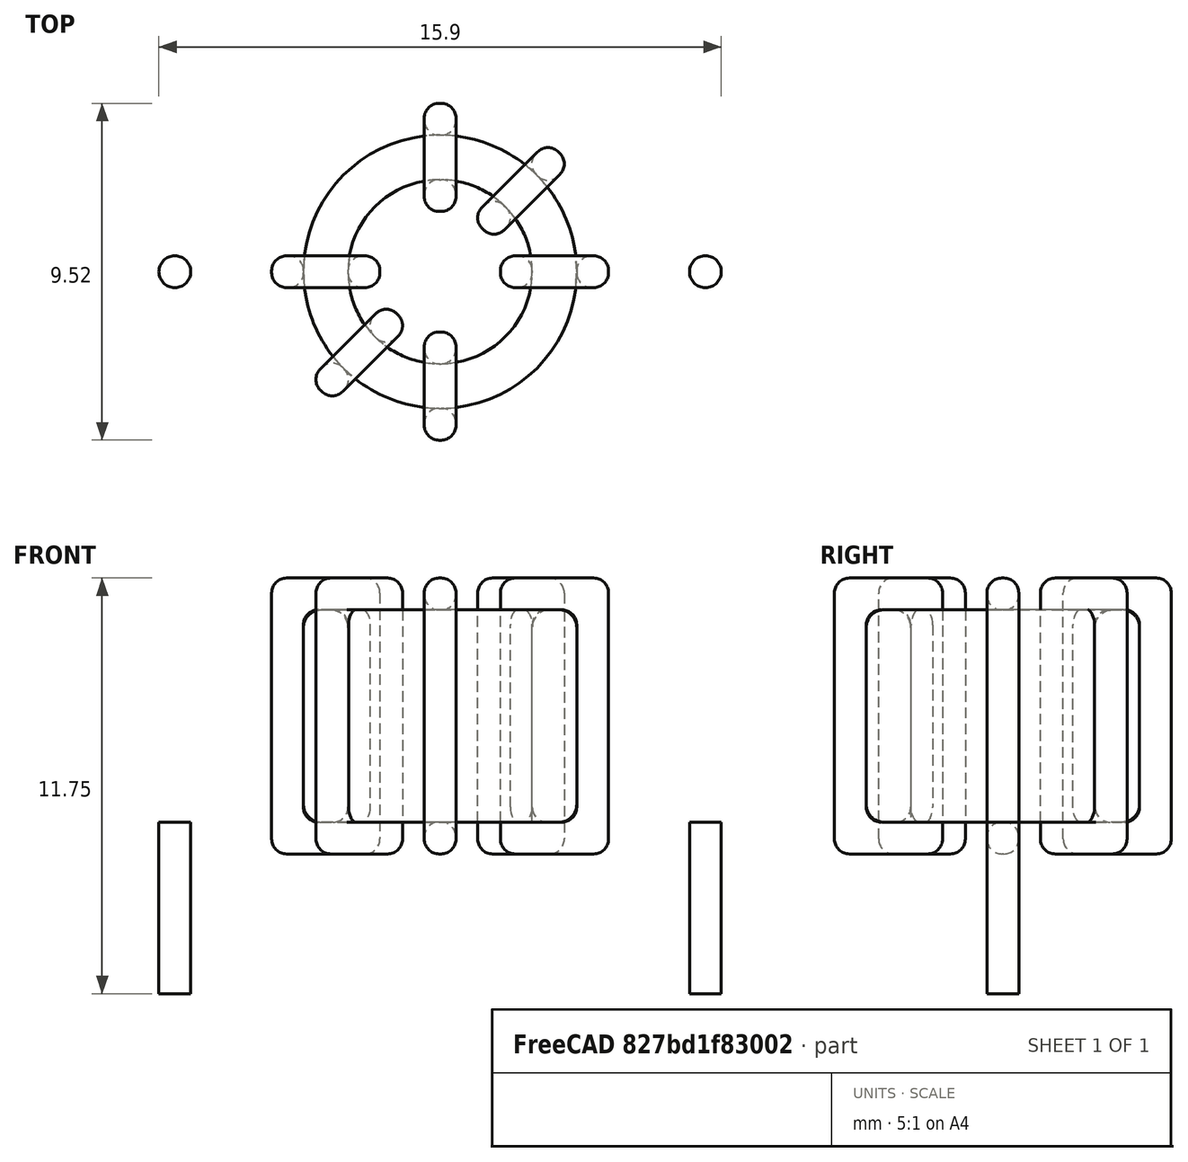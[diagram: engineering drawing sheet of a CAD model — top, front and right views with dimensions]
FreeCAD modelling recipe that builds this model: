
FCSTD DOCUMENT  (FreeCAD 0.16R6703 (Git))
Label: L_Toroid_Horizontal_D9.5mm_P15.00mm_Diameter10-5mm_Amidon-T37
License: All rights reserved
LicenseURL: http://en.wikipedia.org/wiki/All_rights_reserved
objects: Sketcher::SketchObject×6, PartDesign::Pad×6, PartDesign::Fillet×5, Spreadsheet::Sheet×1
note: 23 computed .brp shape members not serialized (recipe doc carries the construction recipe); baked Part::Feature solids carry a one-line shape summary decoded from their .brp

FEATURE [Spreadsheet::Sheet] Spreadsheet  label="dimensions"
  cells = A1=Wx; B1(Wx)=9.524999999999999; C1(WW)=5.206999999999999; D1=9.524999999999999; A2=Wy; B2(Wy)=9.524999999999999; D2=9.524999999999999; A3=RM; B3(RMx)=15; C3(RMy)=0; A4=d_wire; B4(d_wire)=0.8999999999999999; A5=H; B5(H)=6; A6=offsetx; B6(offsetx)=-2.737500000000001
FEATURE [Sketcher::SketchObject] Sketch
  Placement = pos=(0,0,1.4) rot=(0,0,1;0rad)
  expr: Placement.Base.z = 0.5 + Spreadsheet.d_wire
  expr: Constraints[0] = Spreadsheet.Wx / 2 - Spreadsheet.d_wire
  expr: Constraints[4] = Spreadsheet.WW / 2
  expr: Constraints[2] = Spreadsheet.RMy / 2
  expr: Constraints[1] = Spreadsheet.RMx / 2
  sketch-geometry (2):
    g0: Circle CenterX=7.5 CenterY=0 CenterZ=0 NormalX=0 NormalY=0 NormalZ=1 Radius=3.8625
    g1: Circle CenterX=7.5 CenterY=0 CenterZ=0 NormalX=0 NormalY=0 NormalZ=1 Radius=2.6035
  constraints (5):
    c: Radius(g0) = 3.8625
    c: DistanceX(g-1,g0) = 7.5
    c: DistanceY(g-1,g0) = 0
    c: Coincident(g1,g0)
    c: Radius(g1) = 2.6035
FEATURE [PartDesign::Pad] Pad
  Length = 6
  Length2 = 100
  Placement = pos=(0,0,1.4) rot=(0,0,1;0rad)
  Sketch = -> Sketch
  Type = 0
  expr: Length = Spreadsheet.H
FEATURE [Sketcher::SketchObject] Sketch001
  Placement = pos=(0,0,0.95) rot=(0,0,1;0rad)
  expr: Placement.Base.z = 0.5 + Spreadsheet.d_wire * 0.5
  expr: Constraints[4] = Spreadsheet.RMx
  expr: Constraints[2] = Spreadsheet.RMy
  expr: Constraints[1] = Spreadsheet.d_wire / 2
  sketch-geometry (2):
    g0: Circle CenterX=0 CenterY=0 CenterZ=0 NormalX=0 NormalY=0 NormalZ=1 Radius=0.45
    g1: Circle CenterX=15 CenterY=0 CenterZ=0 NormalX=0 NormalY=0 NormalZ=1 Radius=0.45
  constraints (5):
    c: Equal(g0,g1)
    c: Radius(g0) = 0.45
    c: DistanceY(g-1,g1) = 0
    c: Coincident(g0,g-1)
    c: DistanceX(g-1,g1) = 15
FEATURE [PartDesign::Pad] Pad001
  Length = 0.45
  Length2 = 4.4
  Placement = pos=(0,0,0.95) rot=(0,0,1;0rad)
  Reversed = true
  Sketch = -> Sketch001
  Type = 4
  expr: Length2 = 3.5 + Spreadsheet.d_wire
  expr: Length = Spreadsheet.d_wire / 2
FEATURE [PartDesign::Fillet] Fillet
  Base = -> Pad [Edge6,Edge3,Edge2]
  Placement = pos=(0,0,1.4) rot=(0,0,1;0rad)
  Radius = 0.5
FEATURE [Sketcher::SketchObject] Sketch003
  Placement = pos=(7.5,0,0) rot=(1,0,0;1.5708rad)
  expr: Placement.Base.x = Spreadsheet.RMx / 2
  expr: Constraints[49] = Spreadsheet.Wx - Spreadsheet.d_wire * 2
  expr: Constraints[44] = Spreadsheet.d_wire
  expr: Constraints[23] = Spreadsheet.H
  expr: Constraints[22] = Spreadsheet.Wx / 2 - Spreadsheet.d_wire
  expr: Placement.Base.y = Spreadsheet.RMy / 2
  expr: Constraints[21] = (Spreadsheet.Wx - Spreadsheet.WW) / 2 - Spreadsheet.d_wire
  expr: Constraints[19] = Spreadsheet.d_wire
  expr: Constraints[17] = Spreadsheet.d_wire
  expr: Constraints[18] = Spreadsheet.d_wire
  expr: Constraints[16] = Spreadsheet.d_wire
  sketch-geometry (16):
    g0: LineSegment StartX=-1.7035 StartY=0.5 StartZ=0 EndX=-4.7625 EndY=0.5 EndZ=0
    g1: LineSegment StartX=-4.7625 StartY=0.5 StartZ=0 EndX=-4.7625 EndY=8.3 EndZ=0
    g2: LineSegment StartX=-4.7625 StartY=8.3 StartZ=0 EndX=-1.7035 EndY=8.3 EndZ=0
    g3: LineSegment StartX=-1.7035 StartY=8.3 StartZ=0 EndX=-1.7035 EndY=0.5 EndZ=0
    g4: LineSegment StartX=-3.8625 StartY=7.4 StartZ=0 EndX=-2.6035 EndY=7.4 EndZ=0
    g5: LineSegment StartX=-2.6035 StartY=7.4 StartZ=0 EndX=-2.6035 EndY=1.4 EndZ=0
    g6: LineSegment StartX=-2.6035 StartY=1.4 StartZ=0 EndX=-3.8625 EndY=1.4 EndZ=0
    g7: LineSegment StartX=-3.8625 StartY=1.4 StartZ=0 EndX=-3.8625 EndY=7.4 EndZ=0
    g8: LineSegment StartX=1.7035 StartY=8.3 StartZ=0 EndX=4.7625 EndY=8.3 EndZ=0
    g9: LineSegment StartX=4.7625 StartY=8.3 StartZ=0 EndX=4.7625 EndY=0.5 EndZ=0
    g10: LineSegment StartX=4.7625 StartY=0.5 StartZ=0 EndX=1.7035 EndY=0.5 EndZ=0
    g11: LineSegment StartX=1.7035 StartY=0.5 StartZ=0 EndX=1.7035 EndY=8.3 EndZ=0
    g12: LineSegment StartX=2.6035 StartY=7.4 StartZ=0 EndX=3.8625 EndY=7.4 EndZ=0
    g13: LineSegment StartX=3.8625 StartY=7.4 StartZ=0 EndX=3.8625 EndY=1.4 EndZ=0
    g14: LineSegment StartX=3.8625 StartY=1.4 StartZ=0 EndX=2.6035 EndY=1.4 EndZ=0
    g15: LineSegment StartX=2.6035 StartY=1.4 StartZ=0 EndX=2.6035 EndY=7.4 EndZ=0
  constraints (50):
    c: Horizontal(g0)
    c: Coincident(g1,g0)
    c: Vertical(g1)
    c: Coincident(g2,g1)
    c: Horizontal(g2)
    c: Coincident(g3,g2)
    c: Coincident(g3,g0)
    c: Vertical(g3)
    c: Coincident(g4,g5)
    c: Coincident(g5,g6)
    c: Coincident(g6,g7)
    c: Coincident(g7,g4)
    c: Horizontal(g4)
    c: Horizontal(g6)
    c: Vertical(g5)
    c: Vertical(g7)
    c: DistanceX(g1,g4) = 0.9
    c: DistanceY(g4,g1) = 0.9
    c: DistanceX(g5,g0) = 0.9
    c: DistanceY(g0,g5) = 0.9
    c: DistanceY(g-1,g0) = 0.5
    c: DistanceX(g6,g6) = 1.259
    c: DistanceX(g6,g-1) = 3.8625
    c: DistanceY(g7,g7) = 6
    c: Coincident(g8,g9)
    c: Coincident(g9,g10)
    c: Coincident(g10,g11)
    c: Coincident(g11,g8)
    c: Horizontal(g8)
    c: Horizontal(g10)
    c: Vertical(g9)
    c: Vertical(g11)
    c: Coincident(g12,g13)
    c: Coincident(g13,g14)
    c: Coincident(g14,g15)
    c: Coincident(g15,g12)
    c: Horizontal(g12)
    c: Horizontal(g14)
    c: Vertical(g13)
    c: Vertical(g15)
    c: DistanceY(g8,g2) = 0
    c: DistanceY(g10,g0) = 0
    c: DistanceY(g14,g5) = 0
    c: DistanceY(g12,g4) = 0
    c: DistanceX(g8,g12) = 0.9
    c: Equal(g8,g2)
    c: Equal(g12,g4)
    c: Equal(g9,g1)
    c: Equal(g13,g7)
    c: DistanceX(g4,g12) = 7.725
FEATURE [PartDesign::Pad] Pad002
  Length = 0.9
  Length2 = 100
  Midplane = true
  Placement = pos=(7.5,0,0) rot=(1,0,0;1.5708rad)
  Sketch = -> Sketch003
  Type = 0
  expr: Length = Spreadsheet.d_wire
FEATURE [PartDesign::Fillet] Fillet001
  Base = -> Pad002 [Edge38,Edge41,Edge42,Edge43,Edge29,Edge32,Edge33,Edge34,Edge25,Edge35,Edge36,Edge13,Edge14,Edge15,Edge16,Edge17,Edge18,Edge19,Edge1,Edge2,Edge3,Edge4,Edge5,Edge6,Edge7,Edge37,Edge39,Edge40,Edge20,Edge23,Edge24,Edge21,Edge22,Edge8,Edge9,Edge10,Edge11,Edge12,Edge26,Edge27,+8 more]
  Placement = pos=(7.5,0,0) rot=(1,0,0;1.5708rad)
  Radius = 0.423
  expr: Radius = Spreadsheet.d_wire * 0.47
FEATURE [Sketcher::SketchObject] Sketch004
  Placement = pos=(7.5,0,0) rot=(0.862856,0.357407,0.357407;1.71777rad)
  expr: Placement.Base.x = Spreadsheet.RMx / 2
  expr: Constraints[49] = Spreadsheet.Wx - 2 * Spreadsheet.d_wire
  expr: Constraints[44] = Spreadsheet.d_wire
  expr: Constraints[23] = Spreadsheet.H
  expr: Constraints[22] = Spreadsheet.Wx / 2 - Spreadsheet.d_wire
  expr: Placement.Base.y = Spreadsheet.RMy / 2
  expr: Constraints[21] = (Spreadsheet.Wx - Spreadsheet.WW) / 2 - Spreadsheet.d_wire
  expr: Constraints[19] = Spreadsheet.d_wire
  expr: Constraints[17] = Spreadsheet.d_wire
  expr: Constraints[18] = Spreadsheet.d_wire
  expr: Constraints[16] = Spreadsheet.d_wire
  sketch-geometry (16):
    g0: LineSegment StartX=-1.7035 StartY=0.5 StartZ=0 EndX=-4.7625 EndY=0.5 EndZ=0
    g1: LineSegment StartX=-4.7625 StartY=0.5 StartZ=0 EndX=-4.7625 EndY=8.3 EndZ=0
    g2: LineSegment StartX=-4.7625 StartY=8.3 StartZ=0 EndX=-1.7035 EndY=8.3 EndZ=0
    g3: LineSegment StartX=-1.7035 StartY=8.3 StartZ=0 EndX=-1.7035 EndY=0.5 EndZ=0
    g4: LineSegment StartX=-3.8625 StartY=7.4 StartZ=0 EndX=-2.6035 EndY=7.4 EndZ=0
    g5: LineSegment StartX=-2.6035 StartY=7.4 StartZ=0 EndX=-2.6035 EndY=1.4 EndZ=0
    g6: LineSegment StartX=-2.6035 StartY=1.4 StartZ=0 EndX=-3.8625 EndY=1.4 EndZ=0
    g7: LineSegment StartX=-3.8625 StartY=1.4 StartZ=0 EndX=-3.8625 EndY=7.4 EndZ=0
    g8: LineSegment StartX=1.7035 StartY=8.3 StartZ=0 EndX=4.7625 EndY=8.3 EndZ=0
    g9: LineSegment StartX=4.7625 StartY=8.3 StartZ=0 EndX=4.7625 EndY=0.5 EndZ=0
    g10: LineSegment StartX=4.7625 StartY=0.5 StartZ=0 EndX=1.7035 EndY=0.5 EndZ=0
    g11: LineSegment StartX=1.7035 StartY=0.5 StartZ=0 EndX=1.7035 EndY=8.3 EndZ=0
    g12: LineSegment StartX=2.6035 StartY=7.4 StartZ=0 EndX=3.8625 EndY=7.4 EndZ=0
    g13: LineSegment StartX=3.8625 StartY=7.4 StartZ=0 EndX=3.8625 EndY=1.4 EndZ=0
    g14: LineSegment StartX=3.8625 StartY=1.4 StartZ=0 EndX=2.6035 EndY=1.4 EndZ=0
    g15: LineSegment StartX=2.6035 StartY=1.4 StartZ=0 EndX=2.6035 EndY=7.4 EndZ=0
  constraints (50):
    c: Horizontal(g0)
    c: Coincident(g1,g0)
    c: Vertical(g1)
    c: Coincident(g2,g1)
    c: Horizontal(g2)
    c: Coincident(g3,g2)
    c: Coincident(g3,g0)
    c: Vertical(g3)
    c: Coincident(g4,g5)
    c: Coincident(g5,g6)
    c: Coincident(g6,g7)
    c: Coincident(g7,g4)
    c: Horizontal(g4)
    c: Horizontal(g6)
    c: Vertical(g5)
    c: Vertical(g7)
    c: DistanceX(g1,g4) = 0.9
    c: DistanceY(g4,g1) = 0.9
    c: DistanceX(g5,g0) = 0.9
    c: DistanceY(g0,g5) = 0.9
    c: DistanceY(g-1,g0) = 0.5
    c: DistanceX(g6,g6) = 1.259
    c: DistanceX(g6,g-1) = 3.8625
    c: DistanceY(g7,g7) = 6
    c: Coincident(g8,g9)
    c: Coincident(g9,g10)
    c: Coincident(g10,g11)
    c: Coincident(g11,g8)
    c: Horizontal(g8)
    c: Horizontal(g10)
    c: Vertical(g9)
    c: Vertical(g11)
    c: Coincident(g12,g13)
    c: Coincident(g13,g14)
    c: Coincident(g14,g15)
    c: Coincident(g15,g12)
    c: Horizontal(g12)
    c: Horizontal(g14)
    c: Vertical(g13)
    c: Vertical(g15)
    c: DistanceY(g8,g2) = 0
    c: DistanceY(g10,g0) = 0
    c: DistanceY(g14,g5) = 0
    c: DistanceY(g12,g4) = 0
    c: DistanceX(g8,g12) = 0.9
    c: Equal(g8,g2)
    c: Equal(g12,g4)
    c: Equal(g9,g1)
    c: Equal(g13,g7)
    c: DistanceX(g4,g12) = 7.725
FEATURE [PartDesign::Pad] Pad003
  Length = 0.9
  Length2 = 100
  Midplane = true
  Placement = pos=(7.5,0,0) rot=(0.862856,0.357407,0.357407;1.71777rad)
  Sketch = -> Sketch004
  Type = 0
  expr: Length = Spreadsheet.d_wire
FEATURE [PartDesign::Fillet] Fillet002
  Base = -> Pad003 [Edge38,Edge41,Edge42,Edge43,Edge29,Edge32,Edge33,Edge34,Edge25,Edge35,Edge36,Edge13,Edge14,Edge15,Edge16,Edge17,Edge18,Edge19,Edge1,Edge2,Edge3,Edge4,Edge5,Edge6,Edge7,Edge37,Edge39,Edge40,Edge20,Edge23,Edge24,Edge21,Edge22,Edge8,Edge9,Edge10,Edge11,Edge12,Edge26,Edge27,+8 more]
  Placement = pos=(7.5,0,0) rot=(0.862856,0.357407,0.357407;1.71777rad)
  Radius = 0.423
  expr: Radius = Spreadsheet.d_wire * 0.47
FEATURE [Sketcher::SketchObject] Sketch005
  Placement = pos=(7.5,0,0) rot=(0.862856,-0.357407,-0.357407;1.71777rad)
  expr: Placement.Base.x = Spreadsheet.RMx / 2
  expr: Constraints[49] = Spreadsheet.Wx - 2 * Spreadsheet.d_wire
  expr: Constraints[44] = Spreadsheet.d_wire
  expr: Constraints[23] = Spreadsheet.H
  expr: Constraints[22] = Spreadsheet.Wx / 2 - Spreadsheet.d_wire
  expr: Placement.Base.y = Spreadsheet.RMy / 2
  expr: Constraints[21] = (Spreadsheet.Wx - Spreadsheet.WW) / 2 - Spreadsheet.d_wire
  expr: Constraints[19] = Spreadsheet.d_wire
  expr: Constraints[17] = Spreadsheet.d_wire
  expr: Constraints[18] = Spreadsheet.d_wire
  expr: Constraints[16] = Spreadsheet.d_wire
  sketch-geometry (16):
    g0: LineSegment StartX=-1.7035 StartY=0.5 StartZ=0 EndX=-4.7625 EndY=0.5 EndZ=0
    g1: LineSegment StartX=-4.7625 StartY=0.5 StartZ=0 EndX=-4.7625 EndY=8.3 EndZ=0
    g2: LineSegment StartX=-4.7625 StartY=8.3 StartZ=0 EndX=-1.7035 EndY=8.3 EndZ=0
    g3: LineSegment StartX=-1.7035 StartY=8.3 StartZ=0 EndX=-1.7035 EndY=0.5 EndZ=0
    g4: LineSegment StartX=-3.8625 StartY=7.4 StartZ=0 EndX=-2.6035 EndY=7.4 EndZ=0
    g5: LineSegment StartX=-2.6035 StartY=7.4 StartZ=0 EndX=-2.6035 EndY=1.4 EndZ=0
    g6: LineSegment StartX=-2.6035 StartY=1.4 StartZ=0 EndX=-3.8625 EndY=1.4 EndZ=0
    g7: LineSegment StartX=-3.8625 StartY=1.4 StartZ=0 EndX=-3.8625 EndY=7.4 EndZ=0
    g8: LineSegment StartX=1.7035 StartY=8.3 StartZ=0 EndX=4.7625 EndY=8.3 EndZ=0
    g9: LineSegment StartX=4.7625 StartY=8.3 StartZ=0 EndX=4.7625 EndY=0.5 EndZ=0
    g10: LineSegment StartX=4.7625 StartY=0.5 StartZ=0 EndX=1.7035 EndY=0.5 EndZ=0
    g11: LineSegment StartX=1.7035 StartY=0.5 StartZ=0 EndX=1.7035 EndY=8.3 EndZ=0
    g12: LineSegment StartX=2.6035 StartY=7.4 StartZ=0 EndX=3.8625 EndY=7.4 EndZ=0
    g13: LineSegment StartX=3.8625 StartY=7.4 StartZ=0 EndX=3.8625 EndY=1.4 EndZ=0
    g14: LineSegment StartX=3.8625 StartY=1.4 StartZ=0 EndX=2.6035 EndY=1.4 EndZ=0
    g15: LineSegment StartX=2.6035 StartY=1.4 StartZ=0 EndX=2.6035 EndY=7.4 EndZ=0
  constraints (50):
    c: Horizontal(g0)
    c: Coincident(g1,g0)
    c: Vertical(g1)
    c: Coincident(g2,g1)
    c: Horizontal(g2)
    c: Coincident(g3,g2)
    c: Coincident(g3,g0)
    c: Vertical(g3)
    c: Coincident(g4,g5)
    c: Coincident(g5,g6)
    c: Coincident(g6,g7)
    c: Coincident(g7,g4)
    c: Horizontal(g4)
    c: Horizontal(g6)
    c: Vertical(g5)
    c: Vertical(g7)
    c: DistanceX(g1,g4) = 0.9
    c: DistanceY(g4,g1) = 0.9
    c: DistanceX(g5,g0) = 0.9
    c: DistanceY(g0,g5) = 0.9
    c: DistanceY(g-1,g0) = 0.5
    c: DistanceX(g6,g6) = 1.259
    c: DistanceX(g6,g-1) = 3.8625
    c: DistanceY(g7,g7) = 6
    c: Coincident(g8,g9)
    c: Coincident(g9,g10)
    c: Coincident(g10,g11)
    c: Coincident(g11,g8)
    c: Horizontal(g8)
    c: Horizontal(g10)
    c: Vertical(g9)
    c: Vertical(g11)
    c: Coincident(g12,g13)
    c: Coincident(g13,g14)
    c: Coincident(g14,g15)
    c: Coincident(g15,g12)
    c: Horizontal(g12)
    c: Horizontal(g14)
    c: Vertical(g13)
    c: Vertical(g15)
    c: DistanceY(g8,g2) = 0
    c: DistanceY(g10,g0) = 0
    c: DistanceY(g14,g5) = 0
    c: DistanceY(g12,g4) = 0
    c: DistanceX(g8,g12) = 0.9
    c: Equal(g8,g2)
    c: Equal(g12,g4)
    c: Equal(g9,g1)
    c: Equal(g13,g7)
    c: DistanceX(g4,g12) = 7.725
FEATURE [PartDesign::Pad] Pad004
  Length = 0.9
  Length2 = 100
  Midplane = true
  Placement = pos=(7.5,0,0) rot=(0.862856,-0.357407,-0.357407;1.71777rad)
  Sketch = -> Sketch005
  Type = 0
  expr: Length = Spreadsheet.d_wire
FEATURE [PartDesign::Fillet] Fillet003
  Base = -> Pad004 [Edge38,Edge41,Edge42,Edge43,Edge29,Edge32,Edge33,Edge34,Edge25,Edge35,Edge36,Edge13,Edge14,Edge15,Edge16,Edge17,Edge18,Edge19,Edge1,Edge2,Edge3,Edge4,Edge5,Edge6,Edge7,Edge37,Edge39,Edge40,Edge20,Edge23,Edge24,Edge21,Edge22,Edge8,Edge9,Edge10,Edge11,Edge12,Edge26,Edge27,+8 more]
  Placement = pos=(7.5,0,0) rot=(0.862856,-0.357407,-0.357407;1.71777rad)
  Radius = 0.423
  expr: Radius = Spreadsheet.d_wire * 0.47
FEATURE [Sketcher::SketchObject] Sketch006
  Placement = pos=(7.5,0,0) rot=(0.57735,0.57735,0.57735;2.0944rad)
  expr: Placement.Base.x = Spreadsheet.RMx / 2
  expr: Constraints[49] = Spreadsheet.Wx - Spreadsheet.d_wire * 2
  expr: Constraints[44] = Spreadsheet.d_wire
  expr: Constraints[23] = Spreadsheet.H
  expr: Constraints[22] = Spreadsheet.Wx / 2 - Spreadsheet.d_wire
  expr: Placement.Base.y = Spreadsheet.RMy / 2
  expr: Constraints[21] = (Spreadsheet.Wx - Spreadsheet.WW) / 2 - Spreadsheet.d_wire
  expr: Constraints[19] = Spreadsheet.d_wire
  expr: Constraints[17] = Spreadsheet.d_wire
  expr: Constraints[18] = Spreadsheet.d_wire
  expr: Constraints[16] = Spreadsheet.d_wire
  sketch-geometry (16):
    g0: LineSegment StartX=-1.7035 StartY=0.5 StartZ=0 EndX=-4.7625 EndY=0.5 EndZ=0
    g1: LineSegment StartX=-4.7625 StartY=0.5 StartZ=0 EndX=-4.7625 EndY=8.3 EndZ=0
    g2: LineSegment StartX=-4.7625 StartY=8.3 StartZ=0 EndX=-1.7035 EndY=8.3 EndZ=0
    g3: LineSegment StartX=-1.7035 StartY=8.3 StartZ=0 EndX=-1.7035 EndY=0.5 EndZ=0
    g4: LineSegment StartX=-3.8625 StartY=7.4 StartZ=0 EndX=-2.6035 EndY=7.4 EndZ=0
    g5: LineSegment StartX=-2.6035 StartY=7.4 StartZ=0 EndX=-2.6035 EndY=1.4 EndZ=0
    g6: LineSegment StartX=-2.6035 StartY=1.4 StartZ=0 EndX=-3.8625 EndY=1.4 EndZ=0
    g7: LineSegment StartX=-3.8625 StartY=1.4 StartZ=0 EndX=-3.8625 EndY=7.4 EndZ=0
    g8: LineSegment StartX=1.7035 StartY=8.3 StartZ=0 EndX=4.7625 EndY=8.3 EndZ=0
    g9: LineSegment StartX=4.7625 StartY=8.3 StartZ=0 EndX=4.7625 EndY=0.5 EndZ=0
    g10: LineSegment StartX=4.7625 StartY=0.5 StartZ=0 EndX=1.7035 EndY=0.5 EndZ=0
    g11: LineSegment StartX=1.7035 StartY=0.5 StartZ=0 EndX=1.7035 EndY=8.3 EndZ=0
    g12: LineSegment StartX=2.6035 StartY=7.4 StartZ=0 EndX=3.8625 EndY=7.4 EndZ=0
    g13: LineSegment StartX=3.8625 StartY=7.4 StartZ=0 EndX=3.8625 EndY=1.4 EndZ=0
    g14: LineSegment StartX=3.8625 StartY=1.4 StartZ=0 EndX=2.6035 EndY=1.4 EndZ=0
    g15: LineSegment StartX=2.6035 StartY=1.4 StartZ=0 EndX=2.6035 EndY=7.4 EndZ=0
  constraints (50):
    c: Horizontal(g0)
    c: Coincident(g1,g0)
    c: Vertical(g1)
    c: Coincident(g2,g1)
    c: Horizontal(g2)
    c: Coincident(g3,g2)
    c: Coincident(g3,g0)
    c: Vertical(g3)
    c: Coincident(g4,g5)
    c: Coincident(g5,g6)
    c: Coincident(g6,g7)
    c: Coincident(g7,g4)
    c: Horizontal(g4)
    c: Horizontal(g6)
    c: Vertical(g5)
    c: Vertical(g7)
    c: DistanceX(g1,g4) = 0.9
    c: DistanceY(g4,g1) = 0.9
    c: DistanceX(g5,g0) = 0.9
    c: DistanceY(g0,g5) = 0.9
    c: DistanceY(g-1,g0) = 0.5
    c: DistanceX(g6,g6) = 1.259
    c: DistanceX(g6,g-1) = 3.8625
    c: DistanceY(g7,g7) = 6
    c: Coincident(g8,g9)
    c: Coincident(g9,g10)
    c: Coincident(g10,g11)
    c: Coincident(g11,g8)
    c: Horizontal(g8)
    c: Horizontal(g10)
    c: Vertical(g9)
    c: Vertical(g11)
    c: Coincident(g12,g13)
    c: Coincident(g13,g14)
    c: Coincident(g14,g15)
    c: Coincident(g15,g12)
    c: Horizontal(g12)
    c: Horizontal(g14)
    c: Vertical(g13)
    c: Vertical(g15)
    c: DistanceY(g8,g2) = 0
    c: DistanceY(g10,g0) = 0
    c: DistanceY(g14,g5) = 0
    c: DistanceY(g12,g4) = 0
    c: DistanceX(g8,g12) = 0.9
    c: Equal(g8,g2)
    c: Equal(g12,g4)
    c: Equal(g9,g1)
    c: Equal(g13,g7)
    c: DistanceX(g4,g12) = 7.725
FEATURE [PartDesign::Pad] Pad005
  Length = 0.9
  Length2 = 100
  Midplane = true
  Placement = pos=(7.5,0,0) rot=(0.57735,0.57735,0.57735;2.0944rad)
  Sketch = -> Sketch006
  Type = 0
  expr: Length = Spreadsheet.d_wire
FEATURE [PartDesign::Fillet] Fillet004
  Base = -> Pad005 [Edge38,Edge41,Edge42,Edge43,Edge29,Edge32,Edge33,Edge34,Edge25,Edge35,Edge36,Edge13,Edge14,Edge15,Edge16,Edge17,Edge18,Edge19,Edge1,Edge2,Edge3,Edge4,Edge5,Edge6,Edge7,Edge37,Edge39,Edge40,Edge20,Edge23,Edge24,Edge21,Edge22,Edge8,Edge9,Edge10,Edge11,Edge12,Edge26,Edge27,+8 more]
  Placement = pos=(7.5,0,0) rot=(0.57735,0.57735,0.57735;2.0944rad)
  Radius = 0.423
  expr: Radius = Spreadsheet.d_wire * 0.47
